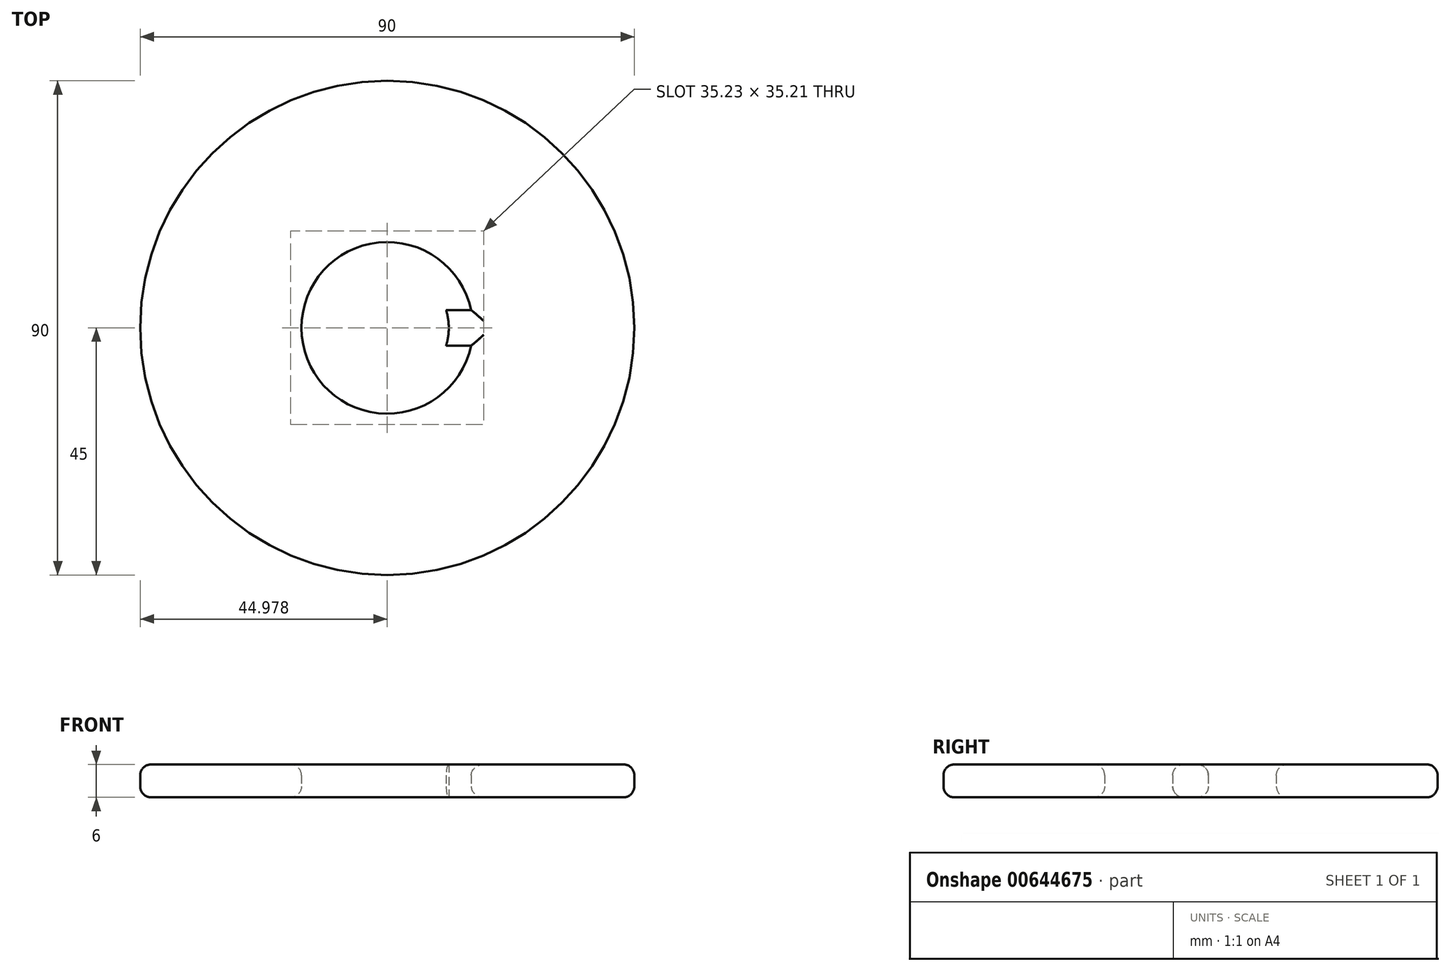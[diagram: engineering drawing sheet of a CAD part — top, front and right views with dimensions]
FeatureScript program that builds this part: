
annotation { "Feature Type Name" : "Feature", "Feature Type Description" : "" }
export const myFeature = defineFeature(function(context is Context, id is Id, definition is map)
    precondition{}
    {
        {
            var Q0;
            Q0=qCreatedBy(makeId("Top.planeOp"),FACE);
            var sketch = newSketch(context, id + "F0", { "sketchPlane" : qUnion([Q0])});
            skCircle(sketch, "E0", {"center": v(0, 0) * mm, "radius": 45 * mm});
            skCircle(sketch, "E1", {"center": v(0, 0) * mm, "radius": 33.16 * mm});
            skLineSegment(sketch, "E2", {"start": v(-33, 3.25) * mm, "end": v(33, 3.25) * mm});
            skLineSegment(sketch, "E3.MirrorCS", {"start": v(-33, -3.25) * mm, "end": v(33, -3.25) * mm});
            skCircle(sketch, "E4", {"center": v(0, 0) * mm, "radius": 11.2 * mm});
            skCircle(sketch, "E5", {"center": v(0, 0) * mm, "radius": 15.63 * mm});
            skSolve(sketch);
        }
        {
            var Q0;
            Q0=makeQuery(id+"F0.imprint","IMPRINT",FACE,{"disambiguationData":[TD([[makeQuery(id+"F0.imprint","IMPRINT",EDGE,{"derivedFrom":sQuery(id+"F0.wireOp",EDGE,"E0")}),1.0]])]});
            var Q1;
            {var subQ0=sQuery(id+"F0.wireOp",EDGE,"E2");var subQ1=sQuery(id+"F0.wireOp",EDGE,"E1");var subQ2=makeQuery(id+"F0.imprint","INTERSECT",VERTEX,{"disambiguationData":[OD(0.0)],"derivedFrom":[subQ1,subQ0]});Q1=makeQuery(id+"F0.imprint","IMPRINT",FACE,{"disambiguationData":[TD([[makeQuery(id+"F0.imprint","IMPRINT",EDGE,{"disambiguationData":[TD([[subQ2,-1.0]])],"derivedFrom":subQ1}),1.0]])]});}
            var Q2;
            {var subQ0=sQuery(id+"F0.wireOp",EDGE,"E5");var subQ1=sQuery(id+"F0.wireOp",EDGE,"E2");var subQ2=makeQuery(id+"F0.imprint","INTERSECT",VERTEX,{"disambiguationData":[OD(0.0)],"derivedFrom":[subQ1,subQ0]});Q2=makeQuery(id+"F0.imprint","IMPRINT",FACE,{"disambiguationData":[TD([[makeQuery(id+"F0.imprint","IMPRINT",EDGE,{"disambiguationData":[TD([[subQ2,-1.0]])],"derivedFrom":subQ1}),-1.0]])]});}
            var Q3;
            {var subQ0=sQuery(id+"F0.wireOp",EDGE,"E5");var subQ1=sQuery(id+"F0.wireOp",EDGE,"E2");var subQ2=makeQuery(id+"F0.imprint","INTERSECT",VERTEX,{"disambiguationData":[OD(0.0)],"derivedFrom":[subQ1,subQ0]});Q3=makeQuery(id+"F0.imprint","IMPRINT",FACE,{"disambiguationData":[TD([[makeQuery(id+"F0.imprint","IMPRINT",EDGE,{"disambiguationData":[TD([[subQ2,-1.0]])],"derivedFrom":subQ1}),1.0]])]});}
            var Q4;
            {var subQ0=sQuery(id+"F0.wireOp",EDGE,"E5");var subQ1=sQuery(id+"F0.wireOp",EDGE,"E3.MirrorCS");var subQ2=makeQuery(id+"F0.imprint","INTERSECT",VERTEX,{"disambiguationData":[OD(0.0)],"derivedFrom":[subQ1,subQ0]});Q4=makeQuery(id+"F0.imprint","IMPRINT",FACE,{"disambiguationData":[TD([[makeQuery(id+"F0.imprint","IMPRINT",EDGE,{"disambiguationData":[TD([[subQ2,-1.0]])],"derivedFrom":subQ1}),-1.0]])]});}
            var Q5;
            {var subQ0=sQuery(id+"F0.wireOp",EDGE,"E4");var subQ1=sQuery(id+"F0.wireOp",EDGE,"E2");var subQ2=makeQuery(id+"F0.imprint","INTERSECT",VERTEX,{"disambiguationData":[OD(1.0)],"derivedFrom":[subQ1,subQ0]});Q5=makeQuery(id+"F0.imprint","IMPRINT",FACE,{"disambiguationData":[TD([[makeQuery(id+"F0.imprint","IMPRINT",EDGE,{"disambiguationData":[TD([[subQ2,-1.0]])],"derivedFrom":subQ1}),-1.0]])]});}
            var Q6;
            {var subQ0=sQuery(id+"F0.wireOp",EDGE,"E2");var subQ1=sQuery(id+"F0.wireOp",EDGE,"E1");var subQ2=makeQuery(id+"F0.imprint","INTERSECT",VERTEX,{"disambiguationData":[OD(1.0)],"derivedFrom":[subQ1,subQ0]});Q6=makeQuery(id+"F0.imprint","IMPRINT",FACE,{"disambiguationData":[TD([[makeQuery(id+"F0.imprint","IMPRINT",EDGE,{"disambiguationData":[TD([[subQ2,1.0]])],"derivedFrom":subQ1}),1.0]])]});}
            extrude(context, id + "F1", {"entities" : qUnion([Q0, Q1, Q2, Q3, Q4, Q5, Q6]), "depth" : 6 * mm, "offsetDistance" : 25.4 * mm});
        }
        {
            var Q0;
            Q0=makeQuery(id+"F1.opExtrude","CAP_EDGE",EDGE,{"disambiguationData":[OSD([sQuery(id+"F0.wireOp",EDGE,"E0")])],"isStart":false});
            var Q1;
            {var subQ0=sQuery(id+"F0.wireOp",EDGE,"E3.MirrorCS");Q1=makeQuery(id+"F1.opExtrude","CAP_EDGE",EDGE,{"disambiguationData":[OSD([subQ0]),TDD([makeQuery(id+"F0.imprint","IMPRINT",EDGE,{"disambiguationData":[TD([[makeQuery(id+"F0.imprint","INTERSECT",VERTEX,{"disambiguationData":[OD(0.0)],"derivedFrom":[sQuery(id+"F0.wireOp",EDGE,"E1"),subQ0]}),-1.0]])],"derivedFrom":subQ0})])],"isStart":false});}
            var Q2;
            {var subQ0=sQuery(id+"F0.wireOp",EDGE,"E5");var subQ1=sQuery(id+"F0.wireOp",EDGE,"E3.MirrorCS");Q2=makeQuery(id+"F1.opExtrude","CAP_EDGE",EDGE,{"disambiguationData":[OSD([subQ0]),TDD([makeQuery(id+"F0.imprint","IMPRINT",EDGE,{"disambiguationData":[TD([[makeQuery(id+"F0.imprint","INTERSECT",VERTEX,{"disambiguationData":[OD(0.0)],"derivedFrom":[subQ1,subQ0]}),-1.0]])],"derivedFrom":subQ0})])],"isStart":true});}
            var Q3;
            {var subQ0=sQuery(id+"F0.wireOp",EDGE,"E3.MirrorCS");Q3=makeQuery(id+"F1.opExtrude","CAP_EDGE",EDGE,{"disambiguationData":[OSD([subQ0]),TDD([makeQuery(id+"F0.imprint","IMPRINT",EDGE,{"disambiguationData":[TD([[makeQuery(id+"F0.imprint","INTERSECT",VERTEX,{"disambiguationData":[OD(1.0)],"derivedFrom":[sQuery(id+"F0.wireOp",EDGE,"E1"),subQ0]}),1.0]])],"derivedFrom":subQ0})])],"isStart":false});}
            var Q4;
            {var subQ0=sQuery(id+"F0.wireOp",EDGE,"E5");var subQ1=sQuery(id+"F0.wireOp",EDGE,"E2");Q4=makeQuery(id+"F1.opExtrude","CAP_EDGE",EDGE,{"disambiguationData":[OSD([subQ0]),TDD([makeQuery(id+"F0.imprint","IMPRINT",EDGE,{"disambiguationData":[TD([[makeQuery(id+"F0.imprint","INTERSECT",VERTEX,{"disambiguationData":[OD(0.0)],"derivedFrom":[subQ1,subQ0]}),1.0]])],"derivedFrom":subQ0})])],"isStart":false});}
            var Q5;
            {var subQ0=sQuery(id+"F0.wireOp",EDGE,"E2");Q5=makeQuery(id+"F1.opExtrude","CAP_EDGE",EDGE,{"disambiguationData":[OSD([subQ0]),TDD([makeQuery(id+"F0.imprint","IMPRINT",EDGE,{"disambiguationData":[TD([[makeQuery(id+"F0.imprint","INTERSECT",VERTEX,{"disambiguationData":[OD(0.0)],"derivedFrom":[sQuery(id+"F0.wireOp",EDGE,"E1"),subQ0]}),-1.0]])],"derivedFrom":subQ0})])],"isStart":false});}
            var Q6;
            {var subQ0=sQuery(id+"F0.wireOp",EDGE,"E2");Q6=makeQuery(id+"F1.opExtrude","CAP_EDGE",EDGE,{"disambiguationData":[OSD([subQ0]),TDD([makeQuery(id+"F0.imprint","IMPRINT",EDGE,{"disambiguationData":[TD([[makeQuery(id+"F0.imprint","INTERSECT",VERTEX,{"disambiguationData":[OD(1.0)],"derivedFrom":[sQuery(id+"F0.wireOp",EDGE,"E1"),subQ0]}),1.0]])],"derivedFrom":subQ0})])],"isStart":false});}
            var Q7;
            Q7=makeQuery(id+"F1.opExtrude","CAP_EDGE",EDGE,{"disambiguationData":[OSD([sQuery(id+"F0.wireOp",EDGE,"E0")])],"isStart":true});
            var Q8;
            {var subQ0=sQuery(id+"F0.wireOp",EDGE,"E5");var subQ1=sQuery(id+"F0.wireOp",EDGE,"E2");Q8=makeQuery(id+"F1.opExtrude","CAP_EDGE",EDGE,{"disambiguationData":[OSD([subQ0]),TDD([makeQuery(id+"F0.imprint","IMPRINT",EDGE,{"disambiguationData":[TD([[makeQuery(id+"F0.imprint","INTERSECT",VERTEX,{"disambiguationData":[OD(0.0)],"derivedFrom":[subQ1,subQ0]}),1.0]])],"derivedFrom":subQ0})])],"isStart":true});}
            var Q9;
            {var subQ0=sQuery(id+"F0.wireOp",EDGE,"E2");Q9=makeQuery(id+"F1.opExtrude","CAP_EDGE",EDGE,{"disambiguationData":[OSD([subQ0]),TDD([makeQuery(id+"F0.imprint","IMPRINT",EDGE,{"disambiguationData":[TD([[makeQuery(id+"F0.imprint","INTERSECT",VERTEX,{"disambiguationData":[OD(1.0)],"derivedFrom":[sQuery(id+"F0.wireOp",EDGE,"E1"),subQ0]}),1.0]])],"derivedFrom":subQ0})])],"isStart":true});}
            var Q10;
            {var subQ0=sQuery(id+"F0.wireOp",EDGE,"E5");var subQ1=sQuery(id+"F0.wireOp",EDGE,"E3.MirrorCS");Q10=makeQuery(id+"F1.opExtrude","CAP_EDGE",EDGE,{"disambiguationData":[OSD([subQ0]),TDD([makeQuery(id+"F0.imprint","IMPRINT",EDGE,{"disambiguationData":[TD([[makeQuery(id+"F0.imprint","INTERSECT",VERTEX,{"disambiguationData":[OD(0.0)],"derivedFrom":[subQ1,subQ0]}),-1.0]])],"derivedFrom":subQ0})])],"isStart":false});}
            var Q11;
            {var subQ0=sQuery(id+"F0.wireOp",EDGE,"E2");Q11=makeQuery(id+"F1.opExtrude","CAP_EDGE",EDGE,{"disambiguationData":[OSD([subQ0]),TDD([makeQuery(id+"F0.imprint","IMPRINT",EDGE,{"disambiguationData":[TD([[makeQuery(id+"F0.imprint","INTERSECT",VERTEX,{"disambiguationData":[OD(0.0)],"derivedFrom":[sQuery(id+"F0.wireOp",EDGE,"E1"),subQ0]}),-1.0]])],"derivedFrom":subQ0})])],"isStart":true});}
            var Q12;
            {var subQ0=sQuery(id+"F0.wireOp",EDGE,"E3.MirrorCS");Q12=makeQuery(id+"F1.opExtrude","CAP_EDGE",EDGE,{"disambiguationData":[OSD([subQ0]),TDD([makeQuery(id+"F0.imprint","IMPRINT",EDGE,{"disambiguationData":[TD([[makeQuery(id+"F0.imprint","INTERSECT",VERTEX,{"disambiguationData":[OD(0.0)],"derivedFrom":[sQuery(id+"F0.wireOp",EDGE,"E1"),subQ0]}),-1.0]])],"derivedFrom":subQ0})])],"isStart":true});}
            var Q13;
            {var subQ0=sQuery(id+"F0.wireOp",EDGE,"E3.MirrorCS");Q13=makeQuery(id+"F1.opExtrude","CAP_EDGE",EDGE,{"disambiguationData":[OSD([subQ0]),TDD([makeQuery(id+"F0.imprint","IMPRINT",EDGE,{"disambiguationData":[TD([[makeQuery(id+"F0.imprint","INTERSECT",VERTEX,{"disambiguationData":[OD(1.0)],"derivedFrom":[sQuery(id+"F0.wireOp",EDGE,"E1"),subQ0]}),1.0]])],"derivedFrom":subQ0})])],"isStart":true});}
            fillet(context, id + "F2", {"entities" : qUnion([Q0, Q1, Q2, Q3, Q4, Q5, Q6, Q7, Q8, Q9, Q10, Q11, Q12, Q13]), "radius" : 2 * mm, "tangentPropagation" : true, "allowEdgeOverflow" : false});
        }
    });
